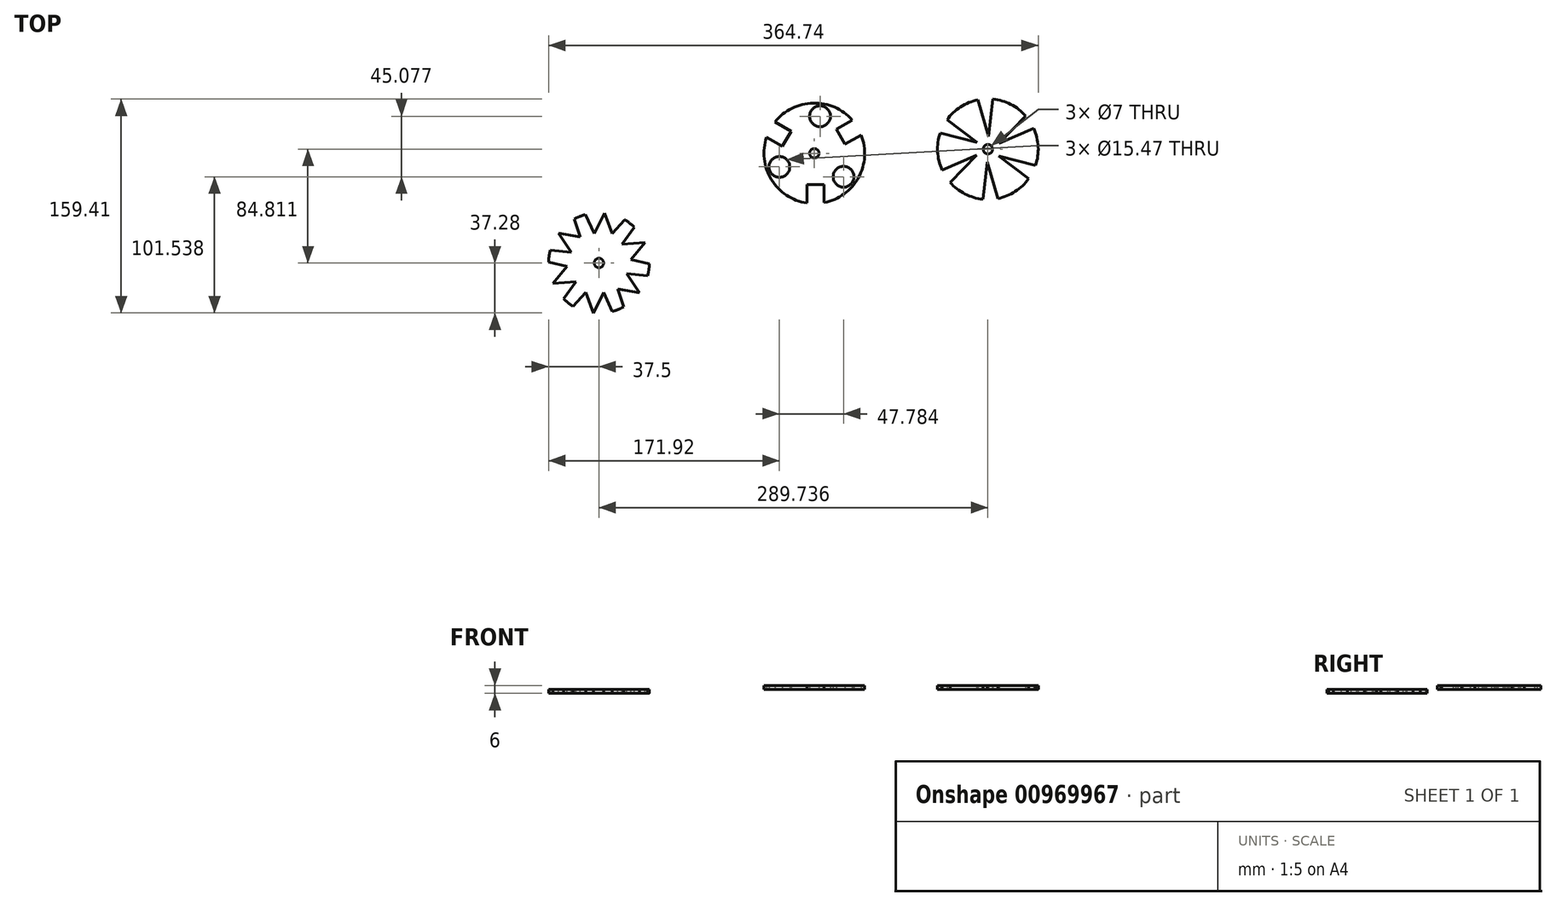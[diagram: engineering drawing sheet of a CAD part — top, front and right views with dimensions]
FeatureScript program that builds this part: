
annotation { "Feature Type Name" : "Feature", "Feature Type Description" : "" }
export const myFeature = defineFeature(function(context is Context, id is Id, definition is map)
    precondition{}
    {
        {
            var Q0;
            Q0=qCreatedBy(makeId("Top.planeOp"),FACE);
            var sketch = newSketch(context, id + "F0", { "sketchPlane" : qUnion([Q0])});
            skLineSegment(sketch, "E0.bottom", {"start": v(-37.5, -37.5) * mm, "end": v(37.5, -37.5) * mm});
            skLineSegment(sketch, "E0.top", {"start": v(-37.5, 37.5) * mm, "end": v(37.5, 37.5) * mm});
            skLineSegment(sketch, "E0.left", {"start": v(-37.5, -37.5) * mm, "end": v(-37.5, 37.5) * mm});
            skLineSegment(sketch, "E0.right", {"start": v(37.5, -37.5) * mm, "end": v(37.5, 37.5) * mm});
            skPoint(sketch, "E0.middle", {"position": v(0, 0) * mm});
            skCircle(sketch, "E1", {"center": v(0, 0) * mm, "radius": 3.5 * mm});
            skCircle(sketch, "E2", {"center": v(0, 0) * mm, "radius": 37.5 * mm});
            skLineSegment(sketch, "E3", {"start": v(-19.19, -32.22) * mm, "end": v(-9.72, -21.8) * mm});
            skLineSegment(sketch, "E4", {"start": v(-9.72, -21.8) * mm, "end": v(-4.03, -37.28) * mm});
            skLineSegment(sketch, "E5", {"start": v(-4.03, -37.28) * mm, "end": v(3.4, -21.8) * mm});
            skLineSegment(sketch, "E6", {"start": v(3.4, -21.8) * mm, "end": v(9.98, -36.15) * mm});
            skLineSegment(sketch, "E7.1.0", {"start": v(20.58, -7.95) * mm, "end": v(36.3, -9.43) * mm});
            skLineSegment(sketch, "E7.1.1", {"start": v(30.27, -22.13) * mm, "end": v(20.58, -7.95) * mm});
            skLineSegment(sketch, "E7.1.2", {"start": v(14.02, -19.32) * mm, "end": v(30.27, -22.13) * mm});
            skLineSegment(sketch, "E7.1.3", {"start": v(18.31, -32.73) * mm, "end": v(14.02, -19.32) * mm});
            skLineSegment(sketch, "E7.2.0", {"start": v(17.18, 13.85) * mm, "end": v(26.31, 26.72) * mm});
            skLineSegment(sketch, "E7.2.1", {"start": v(34.3, 15.15) * mm, "end": v(17.18, 13.85) * mm});
            skLineSegment(sketch, "E7.2.2", {"start": v(23.74, 2.48) * mm, "end": v(34.3, 15.15) * mm});
            skLineSegment(sketch, "E7.2.3", {"start": v(37.5, -0.5) * mm, "end": v(23.74, 2.48) * mm});
            skLineSegment(sketch, "E8.2.3.0", {"start": v(-3.4, 21.8) * mm, "end": v(-9.98, 36.15) * mm});
            skLineSegment(sketch, "E8.3.3.0", {"start": v(4.03, 37.28) * mm, "end": v(-3.4, 21.8) * mm});
            skLineSegment(sketch, "E8.6.3.0", {"start": v(9.72, 21.8) * mm, "end": v(4.03, 37.28) * mm});
            skLineSegment(sketch, "E8.9.3.0", {"start": v(19.19, 32.22) * mm, "end": v(9.72, 21.8) * mm});
            skLineSegment(sketch, "E8.2.4.0", {"start": v(-20.58, 7.95) * mm, "end": v(-36.3, 9.43) * mm});
            skLineSegment(sketch, "E8.3.4.0", {"start": v(-30.27, 22.13) * mm, "end": v(-20.58, 7.95) * mm});
            skLineSegment(sketch, "E8.6.4.0", {"start": v(-14.02, 19.32) * mm, "end": v(-30.27, 22.13) * mm});
            skLineSegment(sketch, "E8.9.4.0", {"start": v(-18.31, 32.73) * mm, "end": v(-14.02, 19.32) * mm});
            skLineSegment(sketch, "E8.2.5.0", {"start": v(-17.18, -13.85) * mm, "end": v(-26.31, -26.72) * mm});
            skLineSegment(sketch, "E8.3.5.0", {"start": v(-34.3, -15.15) * mm, "end": v(-17.18, -13.85) * mm});
            skLineSegment(sketch, "E8.6.5.0", {"start": v(-23.74, -2.48) * mm, "end": v(-34.3, -15.15) * mm});
            skLineSegment(sketch, "E8.9.5.0", {"start": v(-37.5, 0.5) * mm, "end": v(-23.74, -2.48) * mm});
            skSolve(sketch);
        }
        {
            var Q0;
            Q0=makeQuery(id+"F0.imprint","IMPRINT",FACE,{"disambiguationData":[TD([[makeQuery(id+"F0.imprint","IMPRINT",EDGE,{"derivedFrom":sQuery(id+"F0.wireOp",EDGE,"E1")}),-1.0]])]});
            extrude(context, id + "F1", {"entities" : qUnion([Q0]), "oppositeDirection" : true, "depth" : 3 * mm, "offsetDistance" : 25 * mm});
        }
        {
            var Q0;
            Q0=qCreatedBy(makeId("Top.planeOp"),FACE);
            var sketch = newSketch(context, id + "F2", { "sketchPlane" : qUnion([Q0])});
            skLineSegment(sketch, "E9.bottom", {"start": v(122.95, 44.25) * mm, "end": v(197.95, 44.25) * mm});
            skLineSegment(sketch, "E9.top", {"start": v(122.95, 119.25) * mm, "end": v(197.95, 119.25) * mm});
            skLineSegment(sketch, "E9.left", {"start": v(122.95, 44.25) * mm, "end": v(122.95, 119.25) * mm});
            skLineSegment(sketch, "E9.right", {"start": v(197.95, 44.25) * mm, "end": v(197.95, 119.25) * mm});
            skPoint(sketch, "E9.middle", {"position": v(160.45, 81.75) * mm});
            skCircle(sketch, "E10", {"center": v(160.45, 81.75) * mm, "radius": 3.5 * mm});
            skCircle(sketch, "E11", {"center": v(160.45, 81.75) * mm, "radius": 37.5 * mm});
            skLineSegment(sketch, "E12", {"start": v(167.74, 44.96) * mm, "end": v(167.74, 58.53) * mm});
            skLineSegment(sketch, "E13", {"start": v(167.74, 58.53) * mm, "end": v(154.8, 58.53) * mm});
            skLineSegment(sketch, "E14", {"start": v(154.8, 58.53) * mm, "end": v(154.8, 44.25) * mm});
            skLineSegment(sketch, "E15.1.0", {"start": v(-44.96, 167.74) * mm, "end": v(-58.53, 167.74) * mm});
            skLineSegment(sketch, "E15.1.1", {"start": v(-58.53, 167.74) * mm, "end": v(-58.53, 154.8) * mm});
            skLineSegment(sketch, "E15.1.2", {"start": v(-58.53, 154.8) * mm, "end": v(-44.25, 154.8) * mm});
            skLineSegment(sketch, "E15.2.0", {"start": v(-167.74, -44.96) * mm, "end": v(-167.74, -58.53) * mm});
            skLineSegment(sketch, "E15.2.1", {"start": v(-167.74, -58.53) * mm, "end": v(-154.8, -58.53) * mm});
            skLineSegment(sketch, "E15.2.2", {"start": v(-154.8, -58.53) * mm, "end": v(-154.8, -44.25) * mm});
            skLineSegment(sketch, "E15.3.0", {"start": v(44.96, -167.74) * mm, "end": v(58.53, -167.74) * mm});
            skLineSegment(sketch, "E15.3.1", {"start": v(58.53, -167.74) * mm, "end": v(58.53, -154.8) * mm});
            skLineSegment(sketch, "E15.3.2", {"start": v(58.53, -154.8) * mm, "end": v(44.25, -154.8) * mm});
            skPoint(sketch, "E15.center", {"position": v(0, 0) * mm});
            skLineSegment(sketch, "E16.1.0", {"start": v(188.65, 106.46) * mm, "end": v(176.9, 99.67) * mm});
            skLineSegment(sketch, "E16.1.1", {"start": v(176.9, 99.67) * mm, "end": v(183.37, 88.47) * mm});
            skLineSegment(sketch, "E16.1.2", {"start": v(183.37, 88.47) * mm, "end": v(195.74, 95.62) * mm});
            skLineSegment(sketch, "E16.2.0", {"start": v(124.94, 93.82) * mm, "end": v(136.7, 87.04) * mm});
            skLineSegment(sketch, "E16.2.1", {"start": v(136.7, 87.04) * mm, "end": v(143.16, 98.23) * mm});
            skLineSegment(sketch, "E16.2.2", {"start": v(143.16, 98.23) * mm, "end": v(130.79, 105.38) * mm});
            skCircle(sketch, "E17", {"center": v(182.2, 64.26) * mm, "radius": 7.73 * mm});
            skCircle(sketch, "E18.1.0", {"center": v(164.71, 109.33) * mm, "radius": 7.73 * mm});
            skCircle(sketch, "E18.2.0", {"center": v(134.42, 71.65) * mm, "radius": 7.73 * mm});
            skSolve(sketch);
        }
        {
            var Q0;
            Q0=makeQuery(id+"F2.imprint","IMPRINT",FACE,{"disambiguationData":[TD([[makeQuery(id+"F2.imprint","IMPRINT",EDGE,{"derivedFrom":sQuery(id+"F2.wireOp",EDGE,"E10")}),-1.0]])]});
            extrude(context, id + "F3", {"entities" : qUnion([Q0]), "depth" : 3 * mm, "offsetDistance" : 25 * mm});
        }
        {
            var Q0;
            Q0=qCreatedBy(makeId("Top.planeOp"),FACE);
            var sketch = newSketch(context, id + "F4", { "sketchPlane" : qUnion([Q0])});
            skLineSegment(sketch, "E19.bottom", {"start": v(252.24, 122.31) * mm, "end": v(327.24, 122.31) * mm});
            skLineSegment(sketch, "E19.top", {"start": v(252.24, 47.31) * mm, "end": v(327.24, 47.31) * mm});
            skLineSegment(sketch, "E19.left", {"start": v(252.24, 122.31) * mm, "end": v(252.24, 47.31) * mm});
            skLineSegment(sketch, "E19.right", {"start": v(327.24, 122.31) * mm, "end": v(327.24, 47.31) * mm});
            skPoint(sketch, "E19.middle", {"position": v(289.74, 84.81) * mm});
            skCircle(sketch, "E20", {"center": v(289.74, 84.81) * mm, "radius": 3.5 * mm});
            skCircle(sketch, "E21", {"center": v(289.74, 84.81) * mm, "radius": 37.5 * mm});
            skLineSegment(sketch, "E22", {"start": v(297.08, 48.04) * mm, "end": v(289.25, 75.21) * mm});
            skLineSegment(sketch, "E23", {"start": v(289.25, 75.21) * mm, "end": v(286.03, 47.5) * mm});
            skLineSegment(sketch, "E24.1.0", {"start": v(297.8, 79.59) * mm, "end": v(320.2, 62.94) * mm});
            skLineSegment(sketch, "E24.1.1", {"start": v(325.25, 72.78) * mm, "end": v(297.8, 79.59) * mm});
            skLineSegment(sketch, "E24.2.0", {"start": v(298.3, 89.19) * mm, "end": v(323.9, 100.25) * mm});
            skLineSegment(sketch, "E24.2.1", {"start": v(317.91, 109.56) * mm, "end": v(298.3, 89.19) * mm});
            skLineSegment(sketch, "E24.3.0", {"start": v(290.23, 94.41) * mm, "end": v(293.45, 122.13) * mm});
            skLineSegment(sketch, "E24.3.1", {"start": v(282.4, 121.59) * mm, "end": v(290.23, 94.41) * mm});
            skLineSegment(sketch, "E24.4.0", {"start": v(281.67, 90.03) * mm, "end": v(259.28, 106.68) * mm});
            skLineSegment(sketch, "E24.4.1", {"start": v(254.22, 96.84) * mm, "end": v(281.67, 90.03) * mm});
            skLineSegment(sketch, "E24.5.0", {"start": v(281.18, 80.44) * mm, "end": v(255.56, 69.37) * mm});
            skLineSegment(sketch, "E24.5.1", {"start": v(261.56, 60.07) * mm, "end": v(281.18, 80.44) * mm});
            skSolve(sketch);
        }
        {
            var Q0;
            Q0=makeQuery(id+"F4.imprint","IMPRINT",FACE,{"disambiguationData":[TD([[makeQuery(id+"F4.imprint","IMPRINT",EDGE,{"derivedFrom":sQuery(id+"F4.wireOp",EDGE,"E20")}),-1.0]])]});
            extrude(context, id + "F5", {"entities" : qUnion([Q0]), "depth" : 3 * mm, "offsetDistance" : 25 * mm});
        }
    });
